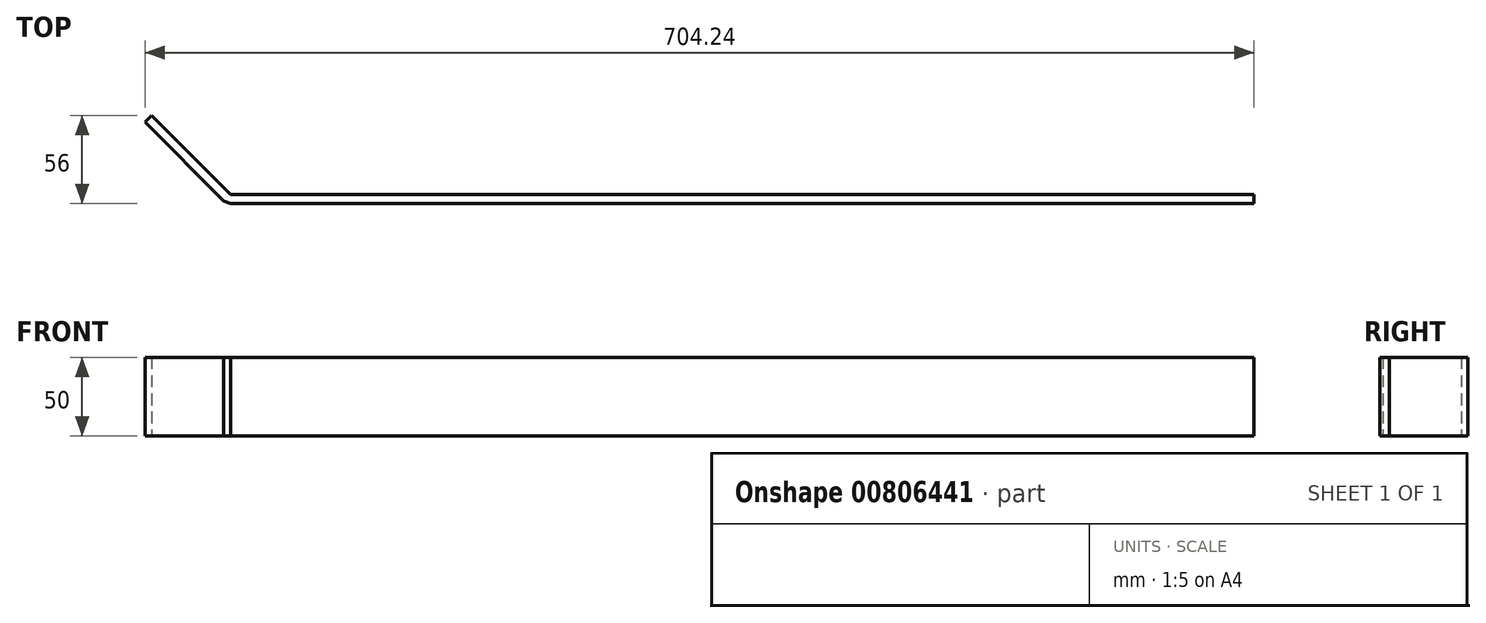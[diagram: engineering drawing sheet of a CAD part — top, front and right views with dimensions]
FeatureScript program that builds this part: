
annotation { "Feature Type Name" : "Feature", "Feature Type Description" : "" }
export const myFeature = defineFeature(function(context is Context, id is Id, definition is map)
    precondition{}
    {
        {
            var Q0;
            Q0=qCreatedBy(makeId("Top.planeOp"),FACE);
            var sketch = newSketch(context, id + "F0", { "sketchPlane" : qUnion([Q0])});
            skLineSegment(sketch, "E0.bottom", {"start": v(325, 3) * mm, "end": v(-325, 3) * mm});
            skLineSegment(sketch, "E0.top", {"start": v(325, -3) * mm, "end": v(-325, -3) * mm});
            skLineSegment(sketch, "E0.left", {"start": v(325, 3) * mm, "end": v(325, -3) * mm});
            skLineSegment(sketch, "E0.right", {"start": v(-325, 3) * mm, "end": v(-325, -3) * mm});
            skPoint(sketch, "E0.middle", {"position": v(0, 0) * mm});
            skLineSegment(sketch, "E1", {"start": v(-325, 3) * mm, "end": v(-325, 53) * mm, "construction": true});
            skLineSegment(sketch, "E2", {"start": v(-325, 53) * mm, "end": v(-375, 53) * mm, "construction": true});
            skLineSegment(sketch, "E3", {"start": v(-325, 3) * mm, "end": v(-375, 53) * mm});
            skLineSegment(sketch, "E4.0", {"start": v(-329.24, -1.24) * mm, "end": v(-379.24, 48.76) * mm});
            skLineSegment(sketch, "E5", {"start": v(-325, -3) * mm, "end": v(-329.24, -1.24) * mm});
            skLineSegment(sketch, "E6", {"start": v(-379.24, 48.76) * mm, "end": v(-375, 53) * mm});
            skSolve(sketch);
        }
        {
            var Q0;
            Q0=makeQuery(id+"F0.imprint","IMPRINT",FACE,{"disambiguationData":[TD([[makeQuery(id+"F0.imprint","IMPRINT",EDGE,{"derivedFrom":sQuery(id+"F0.wireOp",EDGE,"E0.bottom")}),1.0]])]});
            var Q1;
            Q1=makeQuery(id+"F0.imprint","IMPRINT",FACE,{"disambiguationData":[TD([[makeQuery(id+"F0.imprint","IMPRINT",EDGE,{"derivedFrom":sQuery(id+"F0.wireOp",EDGE,"E0.right")}),-1.0]])]});
            extrude(context, id + "F1", {"entities" : qUnion([Q0, Q1]), "depth" : 50 * mm, "offsetDistance" : 25 * mm});
        }
    });
